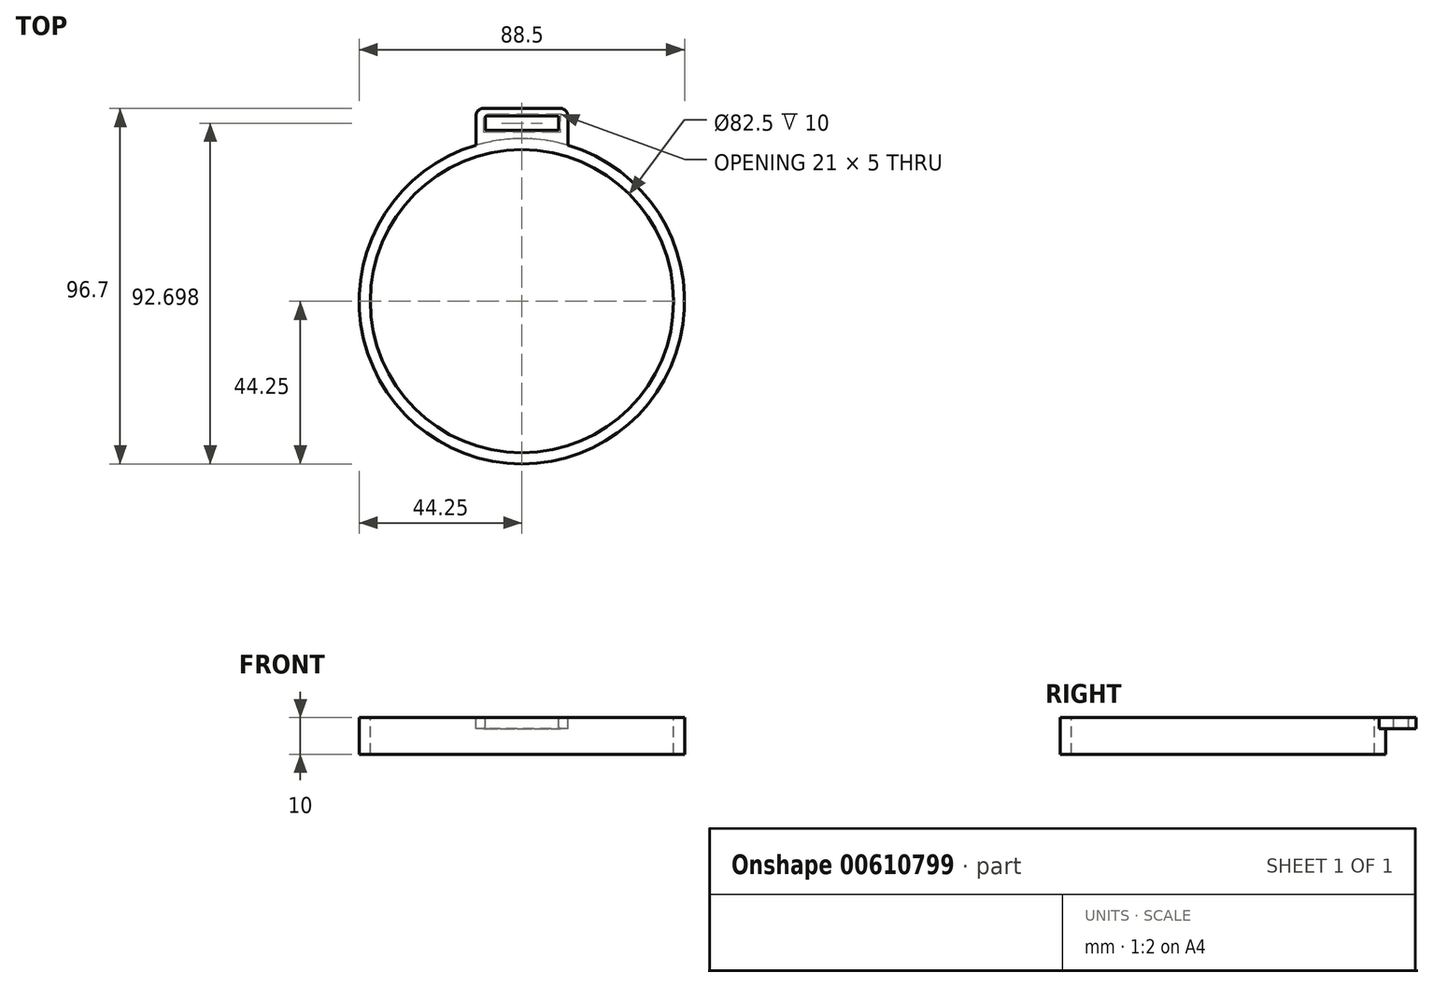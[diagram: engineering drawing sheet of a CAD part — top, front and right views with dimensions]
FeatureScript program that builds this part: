
annotation { "Feature Type Name" : "Feature", "Feature Type Description" : "" }
export const myFeature = defineFeature(function(context is Context, id is Id, definition is map)
    precondition{}
    {
        {
            var Q0;
            Q0=qCreatedBy(makeId("Top.planeOp"),FACE);
            var sketch = newSketch(context, id + "F0", { "sketchPlane" : qUnion([Q0])});
            skCircle(sketch, "E0", {"center": v(0, 0) * mm, "radius": 44.25 * mm});
            skSolve(sketch);
        }
        {
            var Q0;
            Q0=qSketchRegion(id+"F0",true);
            extrude(context, id + "F1", {"entities" : qUnion([Q0]), "depth" : 10 * mm, "offsetDistance" : 25 * mm});
        }
        {
            var Q0;
            Q0=makeQuery(id+"F1.opExtrude","CAP_FACE",FACE,{"disambiguationData":[OSD([sQuery(id+"F0.wireOp",EDGE,"E0")])],"isStart":false});
            var sketch = newSketch(context, id + "F2", { "sketchPlane" : qUnion([Q0])});
            skCircle(sketch, "E1", {"center": v(0, 0) * mm, "radius": 41.25 * mm});
            skSolve(sketch);
        }
        {
            var Q0;
            Q0=qSketchRegion(id+"F2",true);
            extrude(context, id + "F3", {"entities" : qUnion([Q0]), "operationType" : NewBodyOperationType.REMOVE, "oppositeDirection" : true, "depth" : 15 * mm, "offsetDistance" : 25 * mm});
        }
        {
            var Q0;
            Q0=makeQuery(id+"F1.opExtrude","CAP_FACE",FACE,{"disambiguationData":[OSD([sQuery(id+"F0.wireOp",EDGE,"E0")])],"isStart":false});
            var sketch = newSketch(context, id + "F4", { "sketchPlane" : qUnion([Q0])});
            skLineSegment(sketch, "E2", {"start": v(0, 54.92) * mm, "end": v(0, 35.88) * mm, "construction": true});
            skLineSegment(sketch, "E3", {"start": v(-12.5, 52.45) * mm, "end": v(12.5, 52.45) * mm});
            skLineSegment(sketch, "E4", {"start": v(12.5, 52.45) * mm, "end": v(12.5, 42.45) * mm});
            skLineSegment(sketch, "E5", {"start": v(-12.5, 52.45) * mm, "end": v(-12.5, 42.45) * mm});
            skPoint(sketch, "E6", {"position": v(0, 52.45) * mm});
            skSolve(sketch);
        }
        {
            var Q0;
            Q0=makeQuery(id+"F4.imprint","IMPRINT",FACE,{"disambiguationData":[TD([[makeQuery(id+"F4.imprint","IMPRINT",EDGE,{"derivedFrom":sQuery(id+"F4.wireOp",EDGE,"E3")}),-1.0]])]});
            extrude(context, id + "F5", {"entities" : qUnion([Q0]), "operationType" : NewBodyOperationType.ADD, "oppositeDirection" : true, "depth" : 3 * mm, "offsetDistance" : 25 * mm});
        }
        {
            var Q0;
            {var subQ0=sQuery(id+"F0.wireOp",EDGE,"E0");Q0=makeQuery(id+"F5.boolean.opBoolean","MERGE",FACE,{"derivedFrom":[makeQuery(id+"F1.opExtrude","CAP_FACE",FACE,{"disambiguationData":[OSD([subQ0])],"isStart":false}),makeQuery(id+"F5.opExtrude","CAP_FACE",FACE,{"disambiguationData":[OSD([subQ0,sQuery(id+"F4.wireOp",EDGE,"E3"),sQuery(id+"F4.wireOp",EDGE,"E4"),sQuery(id+"F4.wireOp",EDGE,"E5")])],"isStart":true})]});}
            var sketch = newSketch(context, id + "F6", { "sketchPlane" : qUnion([Q0])});
            skPoint(sketch, "E7", {"position": v(-10, 50.45) * mm});
            skPoint(sketch, "E8", {"position": v(10, 46.45) * mm});
            skLineSegment(sketch, "E9.bottom", {"start": v(-10, 50.45) * mm, "end": v(10, 50.45) * mm});
            skLineSegment(sketch, "E9.top", {"start": v(-10, 46.45) * mm, "end": v(10, 46.45) * mm});
            skLineSegment(sketch, "E9.left", {"start": v(-10, 50.45) * mm, "end": v(-10, 46.45) * mm});
            skLineSegment(sketch, "E9.right", {"start": v(10, 50.45) * mm, "end": v(10, 46.45) * mm});
            skSolve(sketch);
        }
        {
            var Q0;
            Q0=makeQuery(id+"F6.imprint","IMPRINT",FACE,{"disambiguationData":[TD([[makeQuery(id+"F6.imprint","IMPRINT",EDGE,{"derivedFrom":sQuery(id+"F6.wireOp",EDGE,"E9.bottom")}),-1.0]])]});
            extrude(context, id + "F7", {"entities" : qUnion([Q0]), "operationType" : NewBodyOperationType.REMOVE, "oppositeDirection" : true, "depth" : 25 * mm, "offsetDistance" : 25 * mm});
        }
        {
            var Q0;
            Q0=makeQuery(id+"F5.opExtrude","CAP_EDGE",EDGE,{"disambiguationData":[OSD([sQuery(id+"F0.wireOp",EDGE,"E0")])],"isStart":false});
            var Q1;
            Q1=makeQuery(id+"F5.opExtrude","SWEPT_EDGE",EDGE,{"disambiguationData":[OSD([sQuery(id+"F0.wireOp",EDGE,"E0"),sQuery(id+"F4.wireOp",EDGE,"E4")])]});
            var Q2;
            Q2=makeQuery(id+"F5.opExtrude","SWEPT_EDGE",EDGE,{"disambiguationData":[OSD([sQuery(id+"F4.wireOp",EDGE,"E3"),sQuery(id+"F4.wireOp",EDGE,"E4")])]});
            var Q3;
            Q3=makeQuery(id+"F5.opExtrude","SWEPT_EDGE",EDGE,{"disambiguationData":[OSD([sQuery(id+"F0.wireOp",EDGE,"E0"),sQuery(id+"F4.wireOp",EDGE,"E5")])]});
            var Q4;
            Q4=makeQuery(id+"F5.opExtrude","SWEPT_EDGE",EDGE,{"disambiguationData":[OSD([sQuery(id+"F4.wireOp",EDGE,"E3"),sQuery(id+"F4.wireOp",EDGE,"E5")])]});
            fillet(context, id + "F8", {"entities" : qUnion([Q0, Q1, Q2, Q3, Q4]), "radius" : 2 * mm, "tangentPropagation" : true, "allowEdgeOverflow" : false});
        }
        {
            var Q0;
            Q0=makeQuery(id+"F7.boolean.opBoolean","COPY",FACE,{"derivedFrom":makeQuery(id+"F7.opExtrude","SWEPT_FACE",FACE,{"disambiguationData":[OSD([sQuery(id+"F6.wireOp",EDGE,"E9.top")])]})});
            var Q1;
            Q1=makeQuery(id+"F7.boolean.opBoolean","COPY",FACE,{"derivedFrom":makeQuery(id+"F7.opExtrude","SWEPT_FACE",FACE,{"disambiguationData":[OSD([sQuery(id+"F6.wireOp",EDGE,"E9.left")])]})});
            var Q2;
            Q2=makeQuery(id+"F7.boolean.opBoolean","COPY",FACE,{"derivedFrom":makeQuery(id+"F7.opExtrude","SWEPT_FACE",FACE,{"disambiguationData":[OSD([sQuery(id+"F6.wireOp",EDGE,"E9.bottom")])]})});
            var Q3;
            Q3=makeQuery(id+"F7.boolean.opBoolean","COPY",FACE,{"derivedFrom":makeQuery(id+"F7.opExtrude","SWEPT_FACE",FACE,{"disambiguationData":[OSD([sQuery(id+"F6.wireOp",EDGE,"E9.right")])]})});
            fillet(context, id + "F9", {"entities" : qUnion([Q0, Q1, Q2, Q3]), "radius" : .5 * mm, "tangentPropagation" : true, "allowEdgeOverflow" : false});
        }
    });
